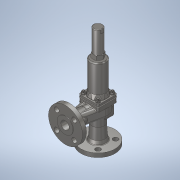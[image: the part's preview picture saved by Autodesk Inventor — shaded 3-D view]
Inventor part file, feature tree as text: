
AUTODESK INVENTOR PART (.ipt)
format: ipt  version: 2021.4 (Build 254397000, 397)  size: 1,174,016 bytes
history: native  units: mm
features: sketch x18, fillet x15, other x14, move_body x7, extrude x6, pattern_circular x6, revolve x4, sweep x4, hole x4, projected_geometry x2, plane x1, chamfer x1
ambient origin geometry x8: Origin, YZ Plane, XZ Plane, XY Plane, X Axis, Y Axis, Z Axis, Center Point
bodies: Solid1 (feature_tree), Solid2 (feature_tree), Solid3 (feature_tree), Solid4 (feature_tree)
feature tree (82):
  other  "ISO 7089 6"
  other  "ISO 4032 M6"
  other  "Stud_M6x30.ipt"
  sketch  "Sketch1"  dims[d0=107.95mm d1=50.8mm]
  revolve  "Revolution1"  [1 undecoded]
  revolve  "Revolution2"  [1 undecoded]
  sweep  "Sweep1"
  sweep  "Sweep2"
  revolve  "Revolution3"  [1 undecoded]
  extrude  "Extrusion1"  Depth=25.0mm
  extrude  "Extrusion2"  Depth=2.4mm
  fillet  "Fillet1"  Radius=7.0mm
  fillet  "Fillet2"  Radius=54.6mm
  fillet  "Fillet3"  Radius=14.3mm
  fillet  "Fillet4"  Radius=48.5mm
  fillet  "Fillet5"  Radius=50.8mm
  fillet  "Fillet9"  Radius=135.0mm
  fillet  "Fillet10"  Radius=24.4mm
  fillet  "Fillet11"  Radius=28.7mm
  fillet  "Fillet12"  Radius=33.139905mm
  fillet  "Fillet13"  Radius=33.139905mm
  fillet  "Fillet14"  Radius=17.0mm
  extrude  "Extrusion3"  Depth=14.0mm
  revolve  "Revolution4"  [1 undecoded]
  hole  "Hole1"  [1 undecoded]
  hole  "Hole2"  [1 undecoded]
  sketch  "Sketch10"  dims[d29=105.0mm d30=107.95mm]
  plane  "Work Plane1"
  sweep  "Sweep3"
  pattern_circular  "Circular Pattern1"  Count=4  [1 undecoded]
  sweep  "Sweep4"
  pattern_circular  "Circular Pattern2"  Angle=90.0deg  [1 undecoded]
  fillet  "Fillet15"  Radius=5.0mm
  fillet  "Fillet16"  Radius=34.0mm
  chamfer  "Chamfer1"  Distance=34.0mm
  fillet  "Fillet17"  Radius=40.0mm
  extrude  "Extrusion4"  TaperAngle=0.0deg  [1 undecoded]
  pattern_circular  "Circular Pattern3"  [2 undecoded]
  hole  "Hole3"  [1 undecoded]
  pattern_circular  "Circular Pattern4"  [2 undecoded]
  hole  "Hole4"  [1 undecoded]
  pattern_circular  "Circular Pattern5"  [2 undecoded]
  fillet  "Fillet18"  Radius=8.0mm
  extrude  "Extrusion5"  Depth=10.0mm
  extrude  "Extrusion6"  Depth=5.0mm
  move_body  "Move Body1"
  other  "Work Axis1"
  move_body  "Move Body2"
  move_body  "Move Body3"
  move_body  "Move Body4"
  move_body  "Move Body5"
  move_body  "Move Body6"
  move_body  "Move Body7"
  pattern_circular  "Circular Pattern6"  [2 undecoded]
  other  "Work Point1"
  other  "Work Point2"
  other  "Work Axis2"
  other  "Work Axis3"
  sketch  "Sketch2"  dims[d2=1.524mm d3=12.7mm]
  sketch  "Sketch3"  dims[d4=105.0mm d5=49.276mm]
  sketch  "Sketch4"  dims[d6=11.5mm d7=44.0mm]
  sketch  "Sketch5"  dims[d8=40.0mm d9=35.0mm]
  sketch  "Sketch6"  dims[d10=62.0mm d11=25.0mm]
  sketch  "Sketch7"  dims[d12=13.0mm d13=2.4mm d14=7.0mm d15=54.6mm d16=14.3mm d17=48.5mm d18=50.8mm d19=135.0mm d20=24.4mm d21=28.7mm d22=33.139905mm d23=33.139905mm d24=17.0mm]
  sketch  "Sketch8"  dims[d25=1.0mm d26=14.0mm]
  sketch  "Sketch9"  dims[d27=28.7mm d28=325.0mm]
  projected_geometry  "Projected Loop1"
  sketch  "Sketch11"  dims[d31=50.8mm d32=1.524mm]
  sketch  "Sketch12"  dims[d33=12.7mm d34=49.276mm]
  projected_geometry  "Projected Loop2"
  sketch  "Sketch13"  dims[d35=44.0mm]
  sketch  "Sketch14"  dims[d36=11.5mm d37=40.0mm]
  sketch  "Sketch15"  dims[d38=35.0mm d39=90.0deg]
  sketch  "Sketch16"  dims[d40=90.0deg]
  sketch  "Sketch17"  dims[d41=0.0mm d42=0.0mm]
  sketch  "Sketch18"  dims[d43=0.0mm d44=0.0mm d45=90.0deg d46=5.0mm d47=34.0mm d48=34.0mm d49=40.0mm d50=0.0mm d51=62.0mm d52=70.0mm d53=34.0mm d54=4.132672mm d55=29.0mm d56=6.0mm d57=0.0mm d58=0.0mm d59=8.0mm d60=8.0mm d61=5.0mm d62=2.0mm d63=2.0mm d67=5.0mm d68=2.0mm d69=2.0mm d70=2.0mm d71=2.0mm d72=0.1mm d73=2.0mm d74=0.1mm d75=2.0mm d76=29.0mm d77=0.0mm d78=28.7mm d79=1.0mm d80=1.0mm d81=90.0deg d82=46.0mm d83=46.0mm d84=7.0mm d85=16.0mm d86=4.0mm d87=2.0mm d88=90.0deg d89=17.1mm d90=20.594885mm d91=4.917mm d92=10.0mm d93=4.0mm d94=2.0mm d95=90.0deg d96=11.1mm d97=20.594885mm d98=12.5mm d99=7.0mm d100=8.0mm d101=90.0deg d102=0.0mm d103=0.0mm d104=40.0mm d105=360.0deg d107=14.0mm d108=0.0mm d109=0.0mm d110=40.0mm d111=360.0deg d113=5.0mm d114=0.5mm d115=3.25mm d116=2.0mm d117=45.0deg d118=2.25mm d119=10.1mm d120=5.0mm d121=11.5mm d122=0.0mm d123=20.0mm d124=360.0deg d126=45.0deg d129=10.0mm d130=4.0mm d131=2.0mm d132=90.0deg d133=11.1mm d134=20.594885mm d135=40.0mm d136=360.0deg d138=79.248mm d139=45.0deg d140=15.875mm d141=10.0mm d142=4.0mm d143=2.0mm d144=90.0deg d145=11.1mm d146=20.594885mm d147=40.0mm d148=360.0deg d150=2.0mm d151=26.67mm d152=11.5mm d153=0.0mm d154=26.67mm d155=11.5mm d156=0.0mm d157=10.0mm d158=23.0mm d159=23.0mm d160=34.4mm d161=90.0deg d162=0.0mm d163=0.0mm d164=1.6mm d165=10.0mm d166=23.0mm d167=23.0mm d168=36.0mm d169=270.0deg d170=1.6mm d171=0.0mm d172=1.6mm d173=10.0mm d174=23.0mm d175=23.0mm d176=24.4mm d177=40.0mm d178=360.0deg]
  other  "Solid1::ISO 7089 6"
  other  "TaggingFeature1"
  other  "Solid1::ISO 4032 M6"
  other  "TaggingFeature2"
  other  "Solid1::Stud_M6x30.ipt"
  other  "TaggingFeature3"
note: 19 required parameter values undecoded (feature->parameter linkage not recoverable at this tier; creation-order binding heuristic only, values carry confidence <= 0.55)